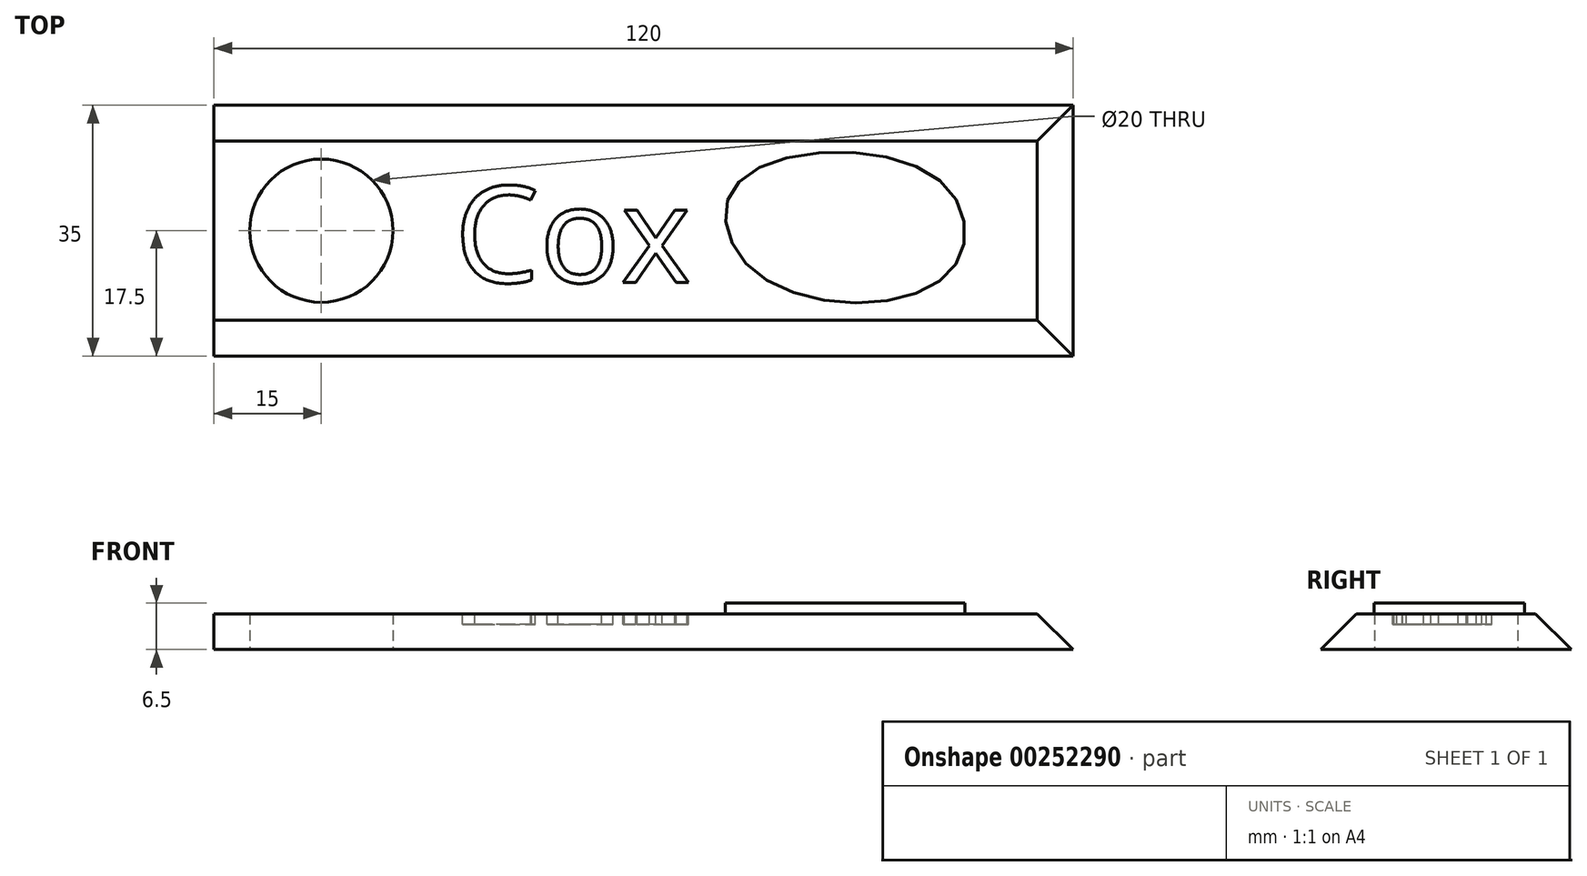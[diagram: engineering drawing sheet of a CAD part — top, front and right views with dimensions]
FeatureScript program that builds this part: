
annotation { "Feature Type Name" : "Feature", "Feature Type Description" : "" }
export const myFeature = defineFeature(function(context is Context, id is Id, definition is map)
    precondition{}
    {
        {
            var Q0;
            Q0=qCreatedBy(makeId("Top.planeOp"),FACE);
            var sketch = newSketch(context, id + "F0", { "sketchPlane" : qUnion([Q0])});
            skLineSegment(sketch, "E0.bottom", {"start": v(-60, 17.5) * mm, "end": v(60, 17.5) * mm});
            skLineSegment(sketch, "E0.top", {"start": v(-60, -17.5) * mm, "end": v(60, -17.5) * mm});
            skLineSegment(sketch, "E0.left", {"start": v(-60, 17.5) * mm, "end": v(-60, -17.5) * mm});
            skLineSegment(sketch, "E0.right", {"start": v(60, 17.5) * mm, "end": v(60, -17.5) * mm});
            skPoint(sketch, "E0.middle", {"position": v(0, 0) * mm});
            skCircle(sketch, "E1", {"center": v(-45, 0) * mm, "radius": 10 * mm});
            skSolve(sketch);
        }
        {
            var Q0;
            Q0=makeQuery(id+"F0.imprint","IMPRINT",FACE,{"disambiguationData":[TD([[makeQuery(id+"F0.imprint","IMPRINT",EDGE,{"derivedFrom":sQuery(id+"F0.wireOp",EDGE,"E0.bottom")}),-1.0]])]});
            extrude(context, id + "F1", {"entities" : qUnion([Q0]), "depth" : 5 * mm});
        }
        {
            var Q0;
            Q0=makeQuery(id+"F1.opExtrude","CAP_EDGE",EDGE,{"disambiguationData":[OSD([sQuery(id+"F0.wireOp",EDGE,"E0.bottom")])],"isStart":false});
            var Q1;
            Q1=makeQuery(id+"F1.opExtrude","CAP_EDGE",EDGE,{"disambiguationData":[OSD([sQuery(id+"F0.wireOp",EDGE,"E0.top")])],"isStart":false});
            var Q2;
            Q2=makeQuery(id+"F1.opExtrude","CAP_EDGE",EDGE,{"disambiguationData":[OSD([sQuery(id+"F0.wireOp",EDGE,"E0.right")])],"isStart":false});
            chamfer(context, id + "F2", {"entities" : qUnion([Q0, Q1, Q2]), "width" : 5 * mm, "tangentPropagation" : true});
        }
        {
            var Q0;
            Q0=makeQuery(id+"F1.opExtrude","CAP_FACE",FACE,{"disambiguationData":[OSD([sQuery(id+"F0.wireOp",EDGE,"E0.bottom"),sQuery(id+"F0.wireOp",EDGE,"E0.top"),sQuery(id+"F0.wireOp",EDGE,"E0.left"),sQuery(id+"F0.wireOp",EDGE,"E0.right"),sQuery(id+"F0.wireOp",EDGE,"E1")])],"isStart":false});
            var sketch = newSketch(context, id + "F3", { "sketchPlane" : qUnion([Q0])});
            skText(sketch, "E2", { "text": "Cox", "fontName": "OpenSans-Regular.ttf"});
            const initialGuessF3  = {"E2": [-0.0264, -0.00722, 1, 0, 0.01353]};
            skSetInitialGuess(sketch, initialGuessF3);
            skSolve(sketch);
        }
        {
            var Q0;
            Q0 = qSketchRegion(id + "F3", true);
            extrude(context, id + "F4", {"entities" : qUnion([Q0]), "operationType" : NewBodyOperationType.REMOVE, "oppositeDirection" : true, "depth" : 1.5 * mm});
        }
        {
            var Q0;
            {var subQ0=sQuery(id+"F0.wireOp",EDGE,"E1");var subQ1=sQuery(id+"F0.wireOp",EDGE,"E0.top");var subQ2=sQuery(id+"F0.wireOp",EDGE,"E0.bottom");var subQ3=sQuery(id+"F0.wireOp",EDGE,"E0.left");var subQ4=sQuery(id+"F0.wireOp",EDGE,"E0.right");Q0=makeQuery(id+"F4.boolean.opBoolean","SPLIT",FACE,{"disambiguationData":[TD([makeQuery(id+"F1.opExtrude","SWEPT_FACE",FACE,{"disambiguationData":[OSD([subQ3])]})])],"derivedFrom":makeQuery(id+"F1.opExtrude","CAP_FACE",FACE,{"disambiguationData":[OSD([subQ2,subQ1,subQ3,subQ4,subQ0])],"isStart":false})});}
            var sketch = newSketch(context, id + "F5", { "sketchPlane" : qUnion([Q0])});
            skFitSpline(sketch, "E3", {"points": [v(13.32, 6.8) * mm, v(40.86, 7.4) * mm, v(42.34, -6.22) * mm, v(16.58, -6.51) * mm, v(13.32, 6.8) * mm]});
            skSolve(sketch);
        }
        {
            var Q0;
            Q0=makeQuery(id+"F5.imprint","IMPRINT",FACE,{"disambiguationData":[TD([[makeQuery(id+"F5.imprint","IMPRINT",EDGE,{"derivedFrom":sQuery(id+"F5.wireOp",EDGE,"E3")}),-1.0]])]});
            extrude(context, id + "F6", {"entities" : qUnion([Q0]), "operationType" : NewBodyOperationType.ADD, "depth" : 1.5 * mm});
        }
    });
